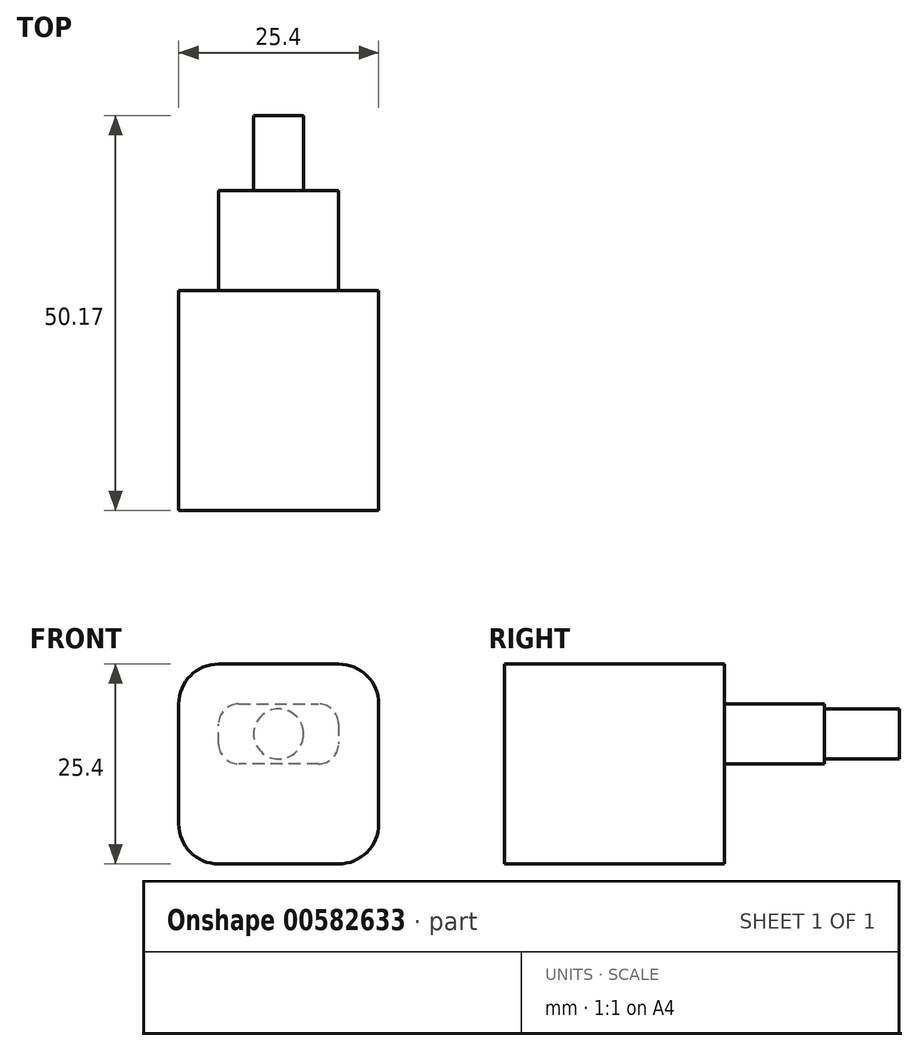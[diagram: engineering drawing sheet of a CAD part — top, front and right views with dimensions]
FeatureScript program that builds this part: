
annotation { "Feature Type Name" : "Feature", "Feature Type Description" : "" }
export const myFeature = defineFeature(function(context is Context, id is Id, definition is map)
    precondition{}
    {
        {
            var Q0;
            Q0=qCreatedBy(makeId("Front.planeOp"),FACE);
            var sketch = newSketch(context, id + "F0", { "sketchPlane" : qUnion([Q0])});
            skLineSegment(sketch, "E0.bottom", {"start": v(0, 0) * mm, "end": v(25.4, 0) * mm});
            skLineSegment(sketch, "E0.top", {"start": v(0, -25.4) * mm, "end": v(25.4, -25.4) * mm});
            skLineSegment(sketch, "E0.left", {"start": v(0, 0) * mm, "end": v(0, -25.4) * mm});
            skLineSegment(sketch, "E0.right", {"start": v(25.4, 0) * mm, "end": v(25.4, -25.4) * mm});
            skSolve(sketch);
        }
        {
            var Q0;
            Q0=makeQuery(id+"F0.imprint","IMPRINT",FACE,{"disambiguationData":[TD([[makeQuery(id+"F0.imprint","IMPRINT",EDGE,{"derivedFrom":sQuery(id+"F0.wireOp",EDGE,"E0.bottom")}),-1.0]])]});
            extrude(context, id + "F1", {"entities" : qUnion([Q0]), "depth" : 27.94 * mm, "offsetDistance" : 25.4 * mm});
        }
        {
            var Q0;
            Q0=makeQuery(id+"F1.opExtrude","SWEPT_EDGE",EDGE,{"disambiguationData":[OSD([sQuery(id+"F0.wireOp",EDGE,"E0.bottom"),sQuery(id+"F0.wireOp",EDGE,"E0.right")])]});
            fillet(context, id + "F2", {"entities" : qUnion([Q0]), "radius" : 5.08 * mm, "tangentPropagation" : true, "allowEdgeOverflow" : false});
        }
        {
            var Q0;
            Q0=makeQuery(id+"F1.opExtrude","SWEPT_EDGE",EDGE,{"disambiguationData":[OSD([sQuery(id+"F0.wireOp",EDGE,"E0.bottom"),sQuery(id+"F0.wireOp",EDGE,"E0.left")])]});
            fillet(context, id + "F3", {"entities" : qUnion([Q0]), "radius" : 5.08 * mm, "tangentPropagation" : true, "allowEdgeOverflow" : false});
        }
        {
            var Q0;
            Q0=makeQuery(id+"F1.opExtrude","SWEPT_EDGE",EDGE,{"disambiguationData":[OSD([sQuery(id+"F0.wireOp",EDGE,"E0.top"),sQuery(id+"F0.wireOp",EDGE,"E0.right")])]});
            fillet(context, id + "F4", {"entities" : qUnion([Q0]), "radius" : 5.08 * mm, "tangentPropagation" : true, "allowEdgeOverflow" : false});
        }
        {
            var Q0;
            Q0=makeQuery(id+"F1.opExtrude","SWEPT_EDGE",EDGE,{"disambiguationData":[OSD([sQuery(id+"F0.wireOp",EDGE,"E0.top"),sQuery(id+"F0.wireOp",EDGE,"E0.left")])]});
            fillet(context, id + "F5", {"entities" : qUnion([Q0]), "radius" : 5.08 * mm, "tangentPropagation" : true, "allowEdgeOverflow" : false});
        }
        {
            var Q0;
            Q0=makeQuery(id+"F1.opExtrude","CAP_FACE",FACE,{"disambiguationData":[OSD([sQuery(id+"F0.wireOp",EDGE,"E0.bottom"),sQuery(id+"F0.wireOp",EDGE,"E0.top"),sQuery(id+"F0.wireOp",EDGE,"E0.left"),sQuery(id+"F0.wireOp",EDGE,"E0.right")])],"isStart":true});
            var sketch = newSketch(context, id + "F6", { "sketchPlane" : qUnion([Q0])});
            skLineSegment(sketch, "E1", {"start": v(-20.32, 0) * mm, "end": v(-20.32, -25.4) * mm});
            skLineSegment(sketch, "E2", {"start": v(-20.32, -25.4) * mm, "end": v(-5.08, -25.4) * mm});
            skLineSegment(sketch, "E3", {"start": v(-5.08, -25.4) * mm, "end": v(-5.08, 0) * mm});
            skLineSegment(sketch, "E4", {"start": v(-5.08, 0) * mm, "end": v(-20.32, 0) * mm});
            skLineSegment(sketch, "E5", {"start": v(0, -5.08) * mm, "end": v(-25.4, -5.08) * mm});
            skLineSegment(sketch, "E6", {"start": v(-25.4, -5.08) * mm, "end": v(-25.4, -12.7) * mm});
            skLineSegment(sketch, "E7", {"start": v(-25.4, -12.7) * mm, "end": v(0, -12.7) * mm});
            skLineSegment(sketch, "E8", {"start": v(0, -12.7) * mm, "end": v(0, -5.08) * mm});
            skSolve(sketch);
        }
        {
            var Q0;
            {var subQ0=sQuery(id+"F6.wireOp",EDGE,"E5");var subQ1=sQuery(id+"F6.wireOp",EDGE,"E1");var subQ2=makeQuery(id+"F6.imprint","INTERSECT",VERTEX,{"derivedFrom":[subQ1,subQ0]});Q0=makeQuery(id+"F6.imprint","IMPRINT",FACE,{"disambiguationData":[TD([[makeQuery(id+"F6.imprint","IMPRINT",EDGE,{"disambiguationData":[TD([[subQ2,-1.0]])],"derivedFrom":subQ1}),1.0]])]});}
            extrude(context, id + "F7", {"entities" : qUnion([Q0]), "operationType" : NewBodyOperationType.ADD, "depth" : 12.7 * mm, "offsetDistance" : 25.4 * mm});
        }
        {
            var Q0;
            Q0=makeQuery(id+"F7.opExtrude","SWEPT_EDGE",EDGE,{"disambiguationData":[OSD([sQuery(id+"F6.wireOp",EDGE,"E3"),sQuery(id+"F6.wireOp",EDGE,"E5")])]});
            fillet(context, id + "F8", {"entities" : qUnion([Q0]), "radius" : 2.54 * mm, "tangentPropagation" : true, "allowEdgeOverflow" : false});
        }
        {
            var Q0;
            Q0=makeQuery(id+"F7.opExtrude","SWEPT_EDGE",EDGE,{"disambiguationData":[OSD([sQuery(id+"F6.wireOp",EDGE,"E3"),sQuery(id+"F6.wireOp",EDGE,"E7")])]});
            fillet(context, id + "F9", {"entities" : qUnion([Q0]), "radius" : 2.54 * mm, "tangentPropagation" : true, "allowEdgeOverflow" : false});
        }
        {
            var Q0;
            Q0=makeQuery(id+"F7.opExtrude","SWEPT_EDGE",EDGE,{"disambiguationData":[OSD([sQuery(id+"F6.wireOp",EDGE,"E1"),sQuery(id+"F6.wireOp",EDGE,"E5")])]});
            fillet(context, id + "F10", {"entities" : qUnion([Q0]), "radius" : 2.54 * mm, "tangentPropagation" : true, "allowEdgeOverflow" : false});
        }
        {
            var Q0;
            Q0=makeQuery(id+"F7.opExtrude","SWEPT_EDGE",EDGE,{"disambiguationData":[OSD([sQuery(id+"F6.wireOp",EDGE,"E1"),sQuery(id+"F6.wireOp",EDGE,"E7")])]});
            fillet(context, id + "F11", {"entities" : qUnion([Q0]), "radius" : 2.54 * mm, "tangentPropagation" : true, "allowEdgeOverflow" : false});
        }
        {
            var Q0;
            Q0=makeQuery(id+"F7.opExtrude","CAP_FACE",FACE,{"disambiguationData":[OSD([sQuery(id+"F6.wireOp",EDGE,"E1"),sQuery(id+"F6.wireOp",EDGE,"E3"),sQuery(id+"F6.wireOp",EDGE,"E5"),sQuery(id+"F6.wireOp",EDGE,"E7")])],"isStart":false});
            var sketch = newSketch(context, id + "F12", { "sketchPlane" : qUnion([Q0])});
            skCircle(sketch, "E9", {"center": v(-12.7, -8.9) * mm, "radius": 3.18 * mm});
            skPoint(sketch, "E9.centerSnap0", {"position": v(-20.32, -8.9) * mm});
            skPoint(sketch, "E9.centerSnap1", {"position": v(-12.7, -5.08) * mm});
            skSolve(sketch);
        }
        {
            var Q0;
            Q0=makeQuery(id+"F12.imprint","IMPRINT",FACE,{"disambiguationData":[TD([[makeQuery(id+"F12.imprint","IMPRINT",EDGE,{"derivedFrom":sQuery(id+"F12.wireOp",EDGE,"E9")}),1.0]])]});
            var sketch = newSketch(context, id + "F13", { "sketchPlane" : qUnion([Q0])});
            skSolve(sketch);
        }
        {
            var Q0;
            Q0 = qSketchRegion(id + "F13", true);
            var Q1;
            Q1=makeQuery(id+"F12.imprint","IMPRINT",FACE,{"disambiguationData":[TD([[makeQuery(id+"F12.imprint","IMPRINT",EDGE,{"derivedFrom":sQuery(id+"F12.wireOp",EDGE,"E9")}),1.0]])]});
            extrude(context, id + "F14", {"entities" : qUnion([Q0, Q1]), "operationType" : NewBodyOperationType.ADD, "depth" : 9.52 * mm, "offsetDistance" : 25.4 * mm});
        }
        {
            var Q0;
            Q0=makeQuery(id+"F14.opExtrude","CAP_FACE",FACE,{"disambiguationData":[OSD([sQuery(id+"F12.wireOp",EDGE,"E9")])],"isStart":false});
            var sketch = newSketch(context, id + "F15", { "sketchPlane" : qUnion([Q0])});
            skCircle(sketch, "E10", {"center": v(-12.7, -8.9) * mm, "radius": 2.54 * mm});
            skSolve(sketch);
        }
    });
